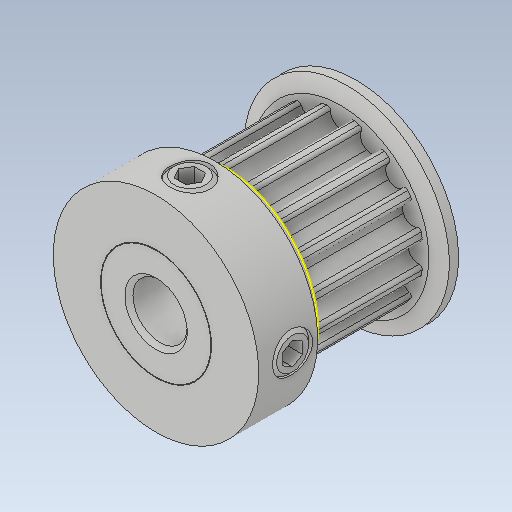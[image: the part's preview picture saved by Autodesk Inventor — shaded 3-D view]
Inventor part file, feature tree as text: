
AUTODESK INVENTOR PART (.ipt)
format: ipt  version: 2020.1 (Build 241239000, 239)  size: 389,120 bytes
history: native  units: mm
features: sketch x1, projected_geometry x1, imported_body x1
ambient origin geometry x8: Origin, YZ Plane, XZ Plane, XY Plane, X Axis, Y Axis, Z Axis, Center Point
bodies: Solid1 (feature_tree)
feature tree (3):
  sketch  "Sketch1"
  projected_geometry  "Projected Loop1"
  imported_body  "Base1"
